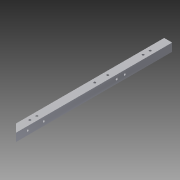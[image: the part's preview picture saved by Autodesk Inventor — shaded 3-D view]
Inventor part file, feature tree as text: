
AUTODESK INVENTOR PART (.ipt)
format: ipt  version: 2014 SP1 (Build 180222100, 222)  size: 116,224 bytes
history: native  units: in
note: dims shown in document units (in); Inventor stores cm internally (conversion verified against a paired STEP export)
features: reference x9, extrude x3, sketch x3
ambient origin geometry x8: Origin, YZ Plane, XZ Plane, XY Plane, X Axis, Y Axis, Z Axis, Center Point
bodies: Solid1 (feature_tree)
feature tree (15):
  extrude  "Extrusion1"  Depth=1.0in
  extrude  "Extrusion2"  Depth=0.0625in TaperAngle=0.0deg
  extrude  "Extrusion3"  Depth=1.0in TaperAngle=0.0deg
  sketch  "Sketch1"  dims[d0=1.0in d1=1.0in]
  sketch  "Sketch2"  dims[d2=0.0625in d3=19.5in d4=0.0in]
  reference  "Reference3"
  reference  "Reference4"
  reference  "Reference5"
  reference  "Reference6"
  sketch  "Sketch3"  dims[d6=45.0deg d7=1.0in d8=0.0in d9=1.0in d10=0.0in]
  reference  "Reference7"
  reference  "Reference8"
  reference  "Reference9"
  reference  "Reference10"
  reference  "Reference11"
